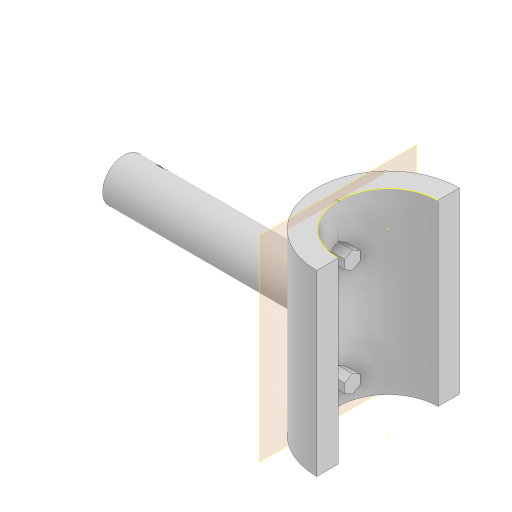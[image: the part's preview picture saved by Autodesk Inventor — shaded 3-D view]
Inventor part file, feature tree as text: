
AUTODESK INVENTOR PART (.ipt)
format: ipt  version: 2024 (Build 280153000, 153)  size: 158,720 bytes
history: native  units: mm
features: sketch x6, extrude x4, plane x1, projected_geometry x1
ambient origin geometry x8: Origin, YZ Plane, XZ Plane, XY Plane, X Axis, Y Axis, Z Axis, Center Point
bodies: Solid1 (feature_tree)
feature tree (12):
  extrude  "Extrusion1"  Depth=20.0mm
  sketch  "Sketch2"  dims[d2=25.0mm d3=0.0mm d4=5.0mm]
  plane  "Work Plane1"
  extrude  "Extrusion2"  Depth=5.0mm
  extrude  "Extrusion3"  Depth=15.0mm
  extrude  "Extrusion4"  Depth=2.0mm TaperAngle=0.0deg
  sketch  "Sketch6"  dims[d11=30.0mm d12=0.0mm d13=3.0mm d14=1.0mm d15=0.0mm d16=0.0mm]
  sketch  "Sketch1"  dims[d0=14.0mm d1=20.0mm]
  sketch  "Sketch3"  dims[d5=1.25mm d6=15.0mm]
  sketch  "Sketch4"  dims[d7=1.25mm d8=2.0mm d9=0.0mm]
  sketch  "Sketch5"  dims[d10=3.0mm]
  projected_geometry  "Projected Loop1"
